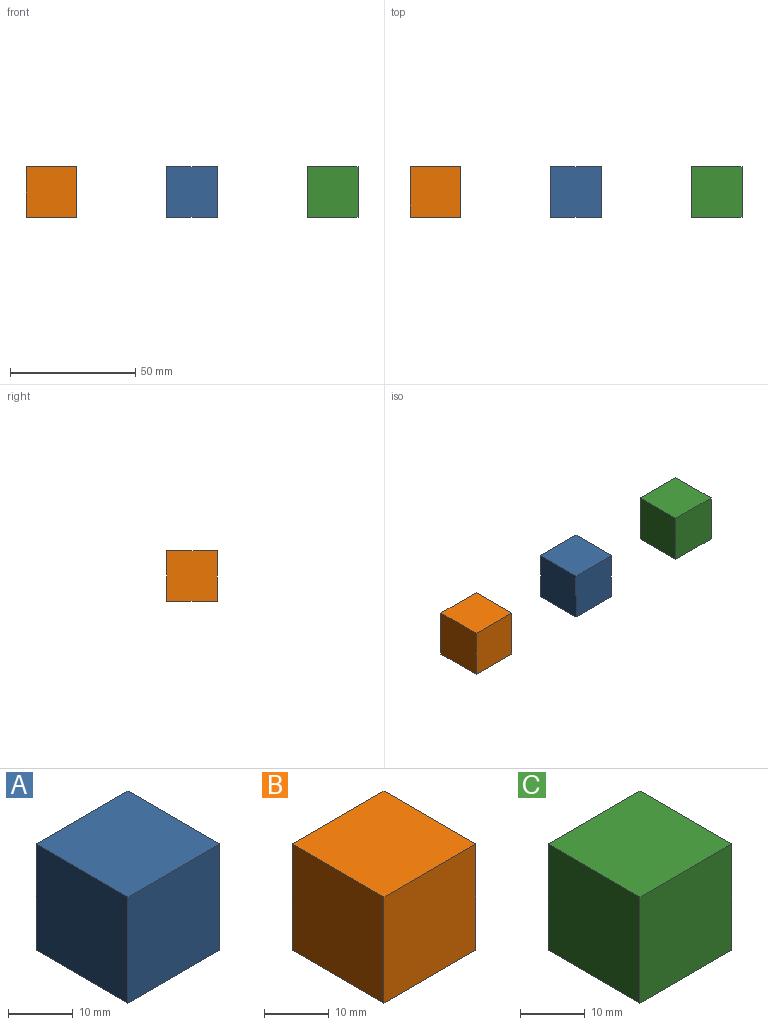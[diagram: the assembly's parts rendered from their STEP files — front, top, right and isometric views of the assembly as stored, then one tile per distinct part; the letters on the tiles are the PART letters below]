
ASSEMBLY  parts=3 mates=2
PART A: 6 faces, bbox 20x20x20 mm
  f0: plane 20x20mm, normal (-1,0,0), area 400mm2, adj f1,f3,f4,f5
  f1: plane 20x20mm, normal (0,0,-1), area 400mm2, adj f0,f2,f4,f5
  f2: plane 20x20mm, normal (1,0,0), area 400mm2, adj f1,f3,f4,f5
  f3: plane 20x20mm, normal (0,0,1), area 400mm2, adj f0,f2,f4,f5
  f4: plane 20x20mm, normal (0,-1,0), area 400mm2, adj f0,f1,f2,f3
  f5: plane 20x20mm, normal (0,1,0), area 400mm2, adj f0,f1,f2,f3
PART B: 6 faces, bbox 20x20x20 mm
  f0: plane 20x20mm, normal (-1,0,0), area 400mm2, adj f1,f3,f4,f5
  f1: plane 20x20mm, normal (0,0,-1), area 400mm2, adj f0,f2,f4,f5
  f2: plane 20x20mm, normal (1,0,0), area 400mm2, adj f1,f3,f4,f5
  f3: plane 20x20mm, normal (0,0,1), area 400mm2, adj f0,f2,f4,f5
  f4: plane 20x20mm, normal (0,-1,0), area 400mm2, adj f0,f1,f2,f3
  f5: plane 20x20mm, normal (0,1,0), area 400mm2, adj f0,f1,f2,f3
PART C: 6 faces, bbox 20x20x20 mm
  f0: plane 20x20mm, normal (-1,0,0), area 400mm2, adj f1,f3,f4,f5
  f1: plane 20x20mm, normal (0,0,-1), area 400mm2, adj f0,f2,f4,f5
  f2: plane 20x20mm, normal (1,0,0), area 400mm2, adj f1,f3,f4,f5
  f3: plane 20x20mm, normal (0,0,1), area 400mm2, adj f0,f2,f4,f5
  f4: plane 20x20mm, normal (0,-1,0), area 400mm2, adj f0,f1,f2,f3
  f5: plane 20x20mm, normal (0,1,0), area 400mm2, adj f0,f1,f2,f3
PLACE A t=(-22.16,36.29,-19.2)mm
PLACE B t=(-98.35,36.29,-19.2)mm
PLACE C t=(54.03,36.29,-19.2)mm
MATE slider A.f2 <-> B.f0  axis (1,0,0) through (17.84,26.29,-9.2)mm
MATE slider C.f2 <-> A.f0  axis (1,0,0) through (74.03,26.29,-9.2)mm
